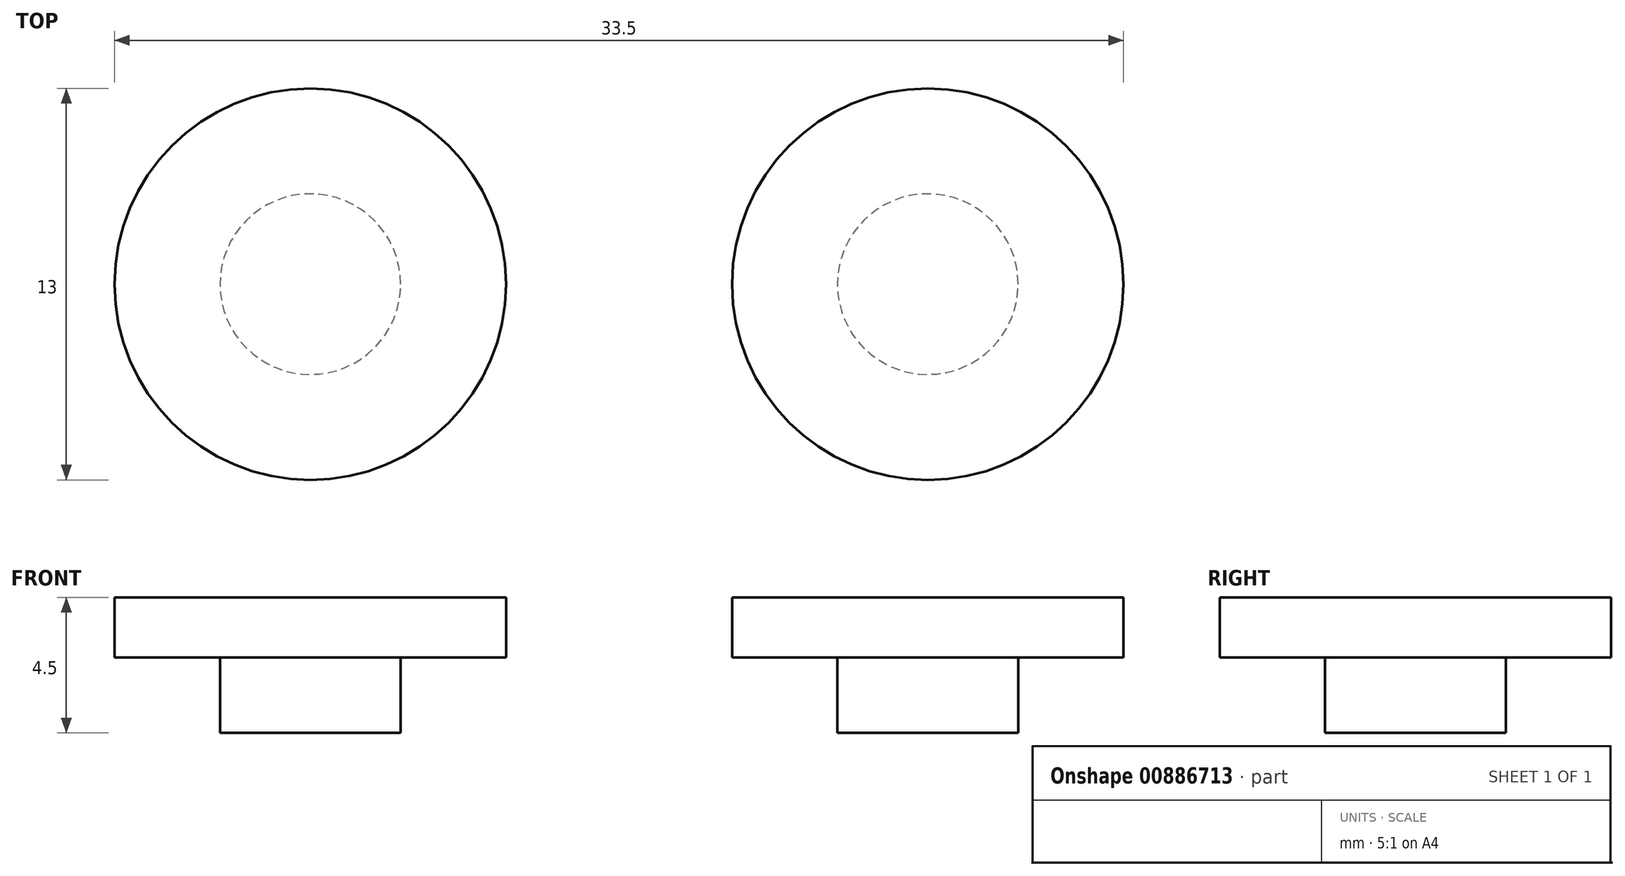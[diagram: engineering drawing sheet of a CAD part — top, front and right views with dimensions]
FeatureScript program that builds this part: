
annotation { "Feature Type Name" : "Feature", "Feature Type Description" : "" }
export const myFeature = defineFeature(function(context is Context, id is Id, definition is map)
    precondition{}
    {
        {
            var Q0;
            Q0=qCreatedBy(makeId("Top.planeOp"),FACE);
            var sketch = newSketch(context, id + "F0", { "sketchPlane" : qUnion([Q0])});
            skCircle(sketch, "E0", {"center": v(0, 0) * mm, "radius": 3 * mm});
            skSolve(sketch);
        }
        {
            var Q0;
            Q0=makeQuery(id+"F0.imprint","IMPRINT",FACE,{"disambiguationData":[TD([[makeQuery(id+"F0.imprint","IMPRINT",EDGE,{"derivedFrom":sQuery(id+"F0.wireOp",EDGE,"E0")}),1.0]])]});
            extrude(context, id + "F1", {"entities" : qUnion([Q0]), "depth" : 2.5 * mm, "offsetDistance" : 25.4 * mm});
        }
        {
            var Q0;
            Q0=makeQuery(id+"F1.opExtrude","CAP_FACE",FACE,{"disambiguationData":[OSD([sQuery(id+"F0.wireOp",EDGE,"E0")])],"isStart":false});
            var sketch = newSketch(context, id + "F2", { "sketchPlane" : qUnion([Q0])});
            skCircle(sketch, "E1", {"center": v(0, 0) * mm, "radius": 6.5 * mm});
            skSolve(sketch);
        }
        {
            var Q0;
            Q0=makeQuery(id+"F2.imprint","IMPRINT",FACE,{"disambiguationData":[TD([[makeQuery(id+"F2.imprint","IMPRINT",EDGE,{"derivedFrom":sQuery(id+"F2.wireOp",EDGE,"E1")}),1.0]])]});
            var Q1;
            Q1=makeQuery(id+"F2.imprint","IMPRINT",FACE,{"disambiguationData":[TD([[makeQuery(id+"F2.imprint","IMPRINT",EDGE,{"derivedFrom":makeQuery(id+"F1.opExtrude","CAP_EDGE",EDGE,{"disambiguationData":[OSD([sQuery(id+"F0.wireOp",EDGE,"E0")])],"isStart":false})}),1.0]])]});
            var Q2;
            Q2=makeQuery(id+"F1.opExtrude","CAP_FACE",FACE,{"disambiguationData":[OSD([sQuery(id+"F0.wireOp",EDGE,"E0")])],"isStart":false});
            var Q3;
            Q3=makeQuery(id+"F1.opExtrude","CAP_FACE",FACE,{"disambiguationData":[OSD([sQuery(id+"F0.wireOp",EDGE,"E0")])],"isStart":true});
            extrude(context, id + "F3", {"entities" : qUnion([Q0, Q1, Q2, Q3]), "operationType" : NewBodyOperationType.ADD, "depth" : 2 * mm, "offsetDistance" : 25.4 * mm});
        }
        {
            var Q0;
            Q0=qCreatedBy(makeId("Top.planeOp"),FACE);
            var sketch = newSketch(context, id + "F4", { "sketchPlane" : qUnion([Q0])});
            skCircle(sketch, "E2", {"center": v(20.5, 0) * mm, "radius": 3 * mm});
            skSolve(sketch);
        }
        {
            var Q0;
            Q0=makeQuery(id+"F4.imprint","IMPRINT",FACE,{"disambiguationData":[TD([[makeQuery(id+"F4.imprint","IMPRINT",EDGE,{"derivedFrom":sQuery(id+"F4.wireOp",EDGE,"E2")}),1.0]])]});
            extrude(context, id + "F5", {"entities" : qUnion([Q0]), "depth" : 2.5 * mm, "offsetDistance" : 25.4 * mm});
        }
        {
            var Q0;
            Q0=makeQuery(id+"F5.opExtrude","CAP_FACE",FACE,{"disambiguationData":[OSD([sQuery(id+"F4.wireOp",EDGE,"E2")])],"isStart":false});
            var sketch = newSketch(context, id + "F6", { "sketchPlane" : qUnion([Q0])});
            skCircle(sketch, "E3", {"center": v(20.5, 0) * mm, "radius": 6.5 * mm});
            skSolve(sketch);
        }
        {
            var Q0;
            Q0=makeQuery(id+"F6.imprint","IMPRINT",FACE,{"disambiguationData":[TD([[makeQuery(id+"F6.imprint","IMPRINT",EDGE,{"derivedFrom":sQuery(id+"F6.wireOp",EDGE,"E3")}),1.0]])]});
            var Q1;
            Q1=makeQuery(id+"F6.imprint","IMPRINT",FACE,{"disambiguationData":[TD([[makeQuery(id+"F6.imprint","IMPRINT",EDGE,{"derivedFrom":makeQuery(id+"F5.opExtrude","CAP_EDGE",EDGE,{"disambiguationData":[OSD([sQuery(id+"F4.wireOp",EDGE,"E2")])],"isStart":false})}),1.0]])]});
            extrude(context, id + "F7", {"entities" : qUnion([Q0, Q1]), "operationType" : NewBodyOperationType.ADD, "depth" : 2 * mm, "offsetDistance" : 25.4 * mm});
        }
    });
